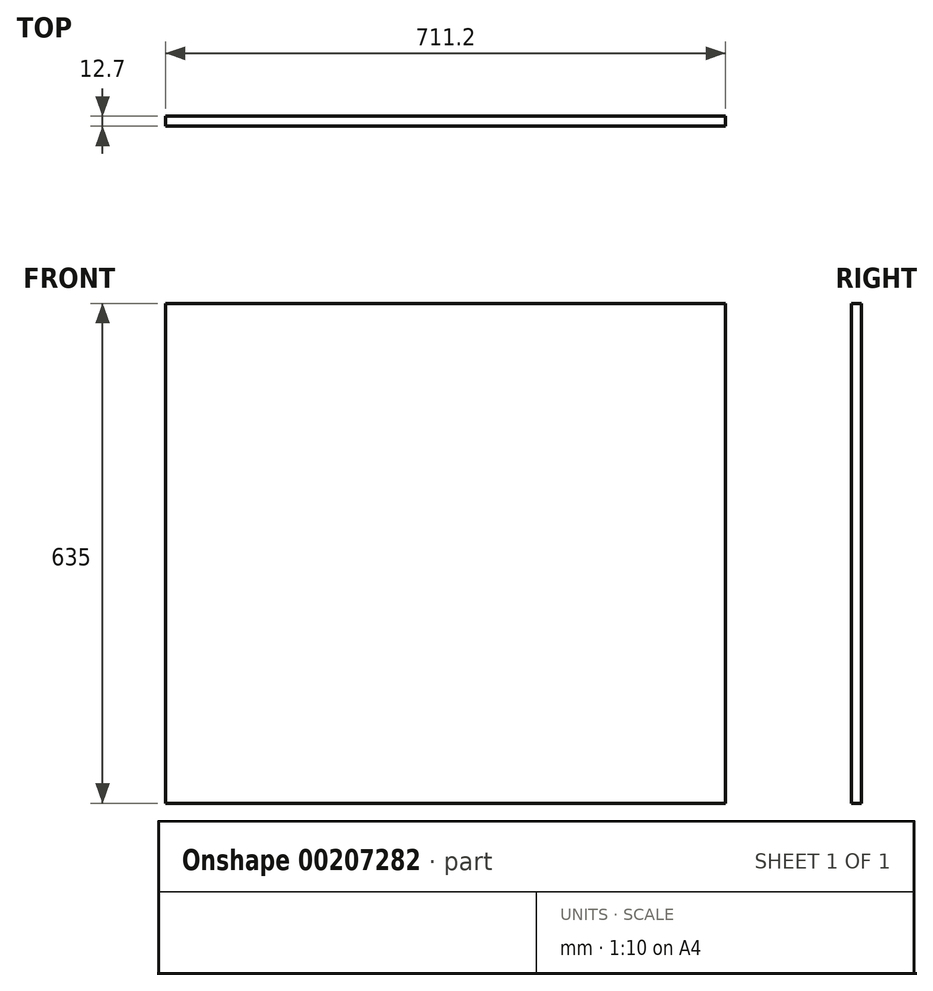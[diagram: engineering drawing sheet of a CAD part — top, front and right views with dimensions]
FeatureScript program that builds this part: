
annotation { "Feature Type Name" : "Feature", "Feature Type Description" : "" }
export const myFeature = defineFeature(function(context is Context, id is Id, definition is map)
    precondition{}
    {
        {
            var Q0;
            Q0=qCreatedBy(makeId("Front.planeOp"),FACE);
            var sketch = newSketch(context, id + "F0", { "sketchPlane" : qUnion([Q0])});
            skLineSegment(sketch, "E0.bottom", {"start": v(-355.6, -317.5) * mm, "end": v(355.6, -317.5) * mm});
            skLineSegment(sketch, "E0.top", {"start": v(-355.6, 317.5) * mm, "end": v(355.6, 317.5) * mm});
            skLineSegment(sketch, "E0.left", {"start": v(-355.6, -317.5) * mm, "end": v(-355.6, 317.5) * mm});
            skLineSegment(sketch, "E0.right", {"start": v(355.6, -317.5) * mm, "end": v(355.6, 317.5) * mm});
            skPoint(sketch, "E0.middle", {"position": v(0, 0) * mm});
            skSolve(sketch);
        }
        {
            var Q0;
            Q0=makeQuery(id+"F0.imprint","IMPRINT",FACE,{"disambiguationData":[TD([[makeQuery(id+"F0.imprint","IMPRINT",EDGE,{"derivedFrom":sQuery(id+"F0.wireOp",EDGE,"E0.bottom")}),1.0]])]});
            extrude(context, id + "F1", {"entities" : qUnion([Q0]), "endBound" : BoundingType.SYMMETRIC, "depth" : 12.7 * mm});
        }
    });
